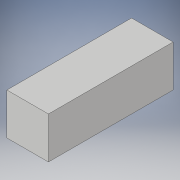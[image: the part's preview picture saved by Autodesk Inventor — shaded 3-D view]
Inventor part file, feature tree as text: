
AUTODESK INVENTOR PART (.ipt)
format: ipt  version: 2017 (Build 210142000, 142)  size: 89,600 bytes
history: native  units: in
note: dims shown in document units (in); Inventor stores cm internally (conversion verified against a paired STEP export)
features: extrude x1, sketch x1
ambient origin geometry x8: Origin, YZ Plane, XZ Plane, XY Plane, X Axis, Y Axis, Z Axis, Center Point
bodies: Solid1 (feature_tree)
feature tree (2):
  extrude  "Extrusion1"  Depth=6.0in
  sketch  "Sketch1"  dims[d0=2.0in d1=6.0in d2=2.0in d3=0.0in]
